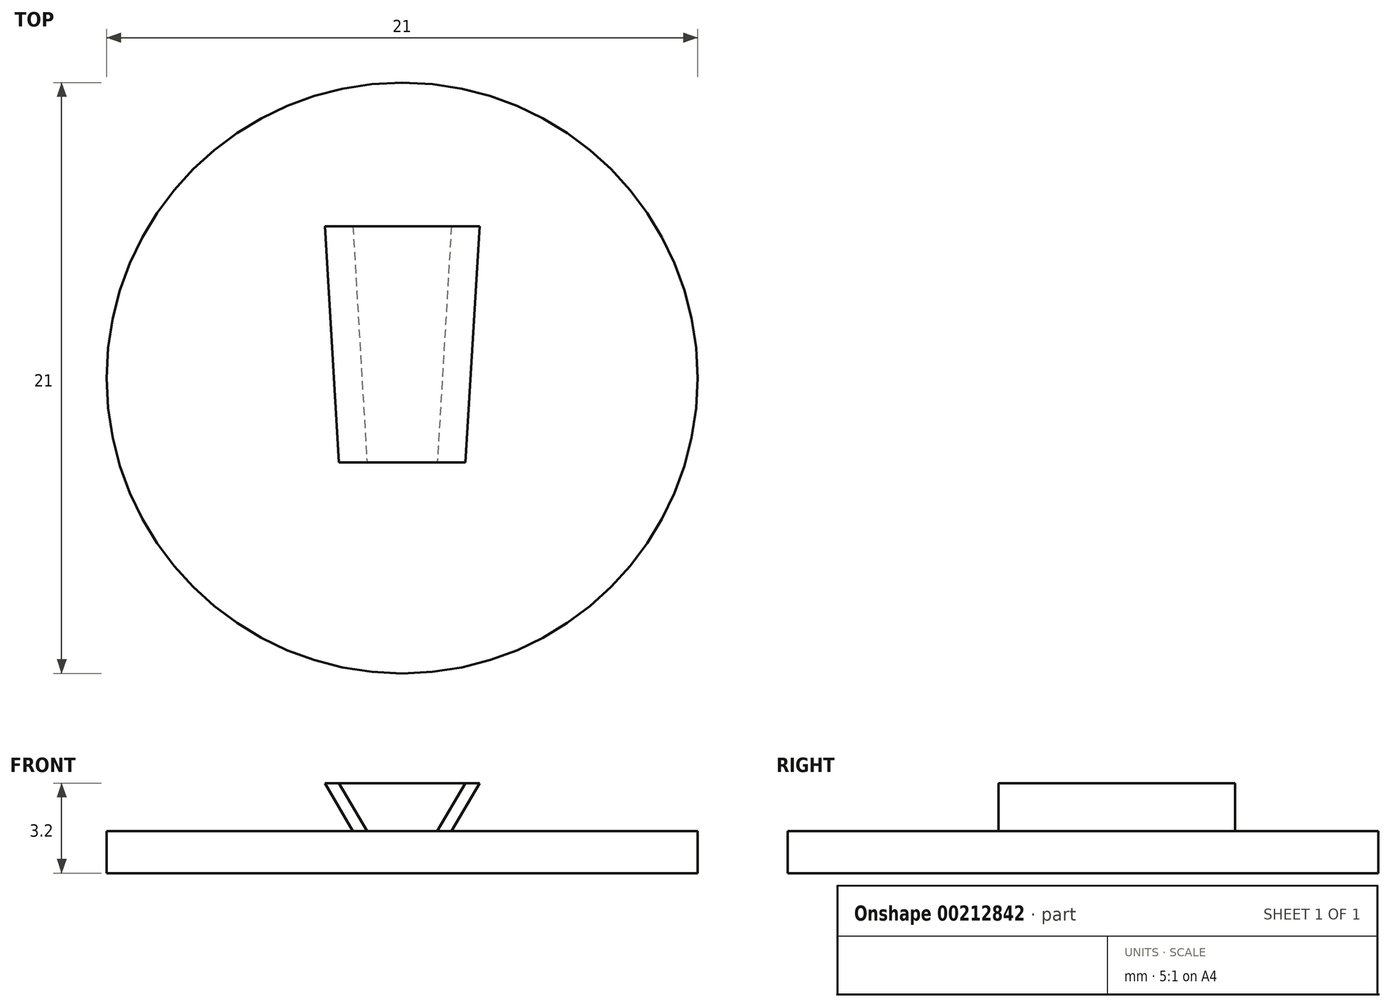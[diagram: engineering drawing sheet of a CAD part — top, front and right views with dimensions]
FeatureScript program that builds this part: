
annotation { "Feature Type Name" : "Feature", "Feature Type Description" : "" }
export const myFeature = defineFeature(function(context is Context, id is Id, definition is map)
    precondition{}
    {
        {
            var Q0;
            Q0=qCreatedBy(makeId("Top.planeOp"),FACE);
            var sketch = newSketch(context, id + "F0", { "sketchPlane" : qUnion([Q0])});
            skCircle(sketch, "E0", {"center": v(0, 0) * mm, "radius": 10.5 * mm});
            skSolve(sketch);
        }
        {
            var Q0;
            Q0=qSketchRegion(id+"F0",true);
            extrude(context, id + "F1", {"entities" : qUnion([Q0]), "oppositeDirection" : true, "depth" : 1.5 * mm});
        }
        {
            var Q0;
            Q0=qCreatedBy(makeId("Front.planeOp"),FACE);
            cPlane(context, id + "F2", {"entities" : qUnion([Q0]), "cplaneType" : CPlaneType.OFFSET, "offset" : 3 * mm, "width" : 150 * mm, "height" : 150 * mm});
        }
        {
            var Q0;
            Q0=qCreatedBy(id+"F2.planeOp",FACE);
            var sketch = newSketch(context, id + "F3", { "sketchPlane" : qUnion([Q0])});
            skLineSegment(sketch, "E1", {"start": v(1.25, 0) * mm, "end": v(2.25, 1.7) * mm});
            skLineSegment(sketch, "E2", {"start": v(2.25, 1.7) * mm, "end": v(-2.25, 1.7) * mm});
            skLineSegment(sketch, "E3", {"start": v(-1.25, 0) * mm, "end": v(1.25, 0) * mm});
            skLineSegment(sketch, "E4.MirrorCS", {"start": v(-1.25, 0) * mm, "end": v(-2.25, 1.7) * mm});
            skSolve(sketch);
        }
        {
            var Q0;
            Q0=qCreatedBy(makeId("Front.planeOp"),FACE);
            cPlane(context, id + "F4", {"entities" : qUnion([Q0]), "cplaneType" : CPlaneType.OFFSET, "offset" : 5.4 * mm, "oppositeDirection" : true, "width" : 150 * mm, "height" : 150 * mm});
        }
        {
            var Q0;
            Q0=qCreatedBy(id+"F4.planeOp",FACE);
            var sketch = newSketch(context, id + "F5", { "sketchPlane" : qUnion([Q0])});
            skLineSegment(sketch, "E5", {"start": v(1.75, 0) * mm, "end": v(2.75, 1.7) * mm});
            skLineSegment(sketch, "E6", {"start": v(2.75, 1.7) * mm, "end": v(-2.75, 1.7) * mm});
            skLineSegment(sketch, "E7", {"start": v(-1.75, 0) * mm, "end": v(1.75, 0) * mm});
            skLineSegment(sketch, "E8.MirrorCS", {"start": v(-1.75, 0) * mm, "end": v(-2.75, 1.7) * mm});
            skSolve(sketch);
        }
        {
            var Q1;
            Q1=qSketchRegion(id+"F5",true);
            var Q2;
            Q2=qSketchRegion(id+"F3",true);
            loft(context, id + "F6", {"operationType" : NewBodyOperationType.ADD, "sheetProfilesArray" : [{ "sheetProfileEntities" : qUnion([Q1]) }, { "sheetProfileEntities" : qUnion([Q2]) }]});
        }
    });
